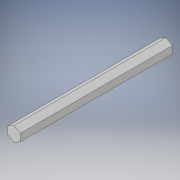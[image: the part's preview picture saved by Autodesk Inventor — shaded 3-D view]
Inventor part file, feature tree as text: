
AUTODESK INVENTOR PART (.ipt)
format: ipt  version: 2018 (Build 220112000, 112)  size: 101,376 bytes
history: native  units: in
note: dims shown in document units (in); Inventor stores cm internally (conversion verified against a paired STEP export)
features: extrude x1, sketch x1
ambient origin geometry x8: Origin, YZ Plane, XZ Plane, XY Plane, X Axis, Y Axis, Z Axis, Center Point
bodies: Solid1 (feature_tree)
feature tree (2):
  extrude  "Extrusion1"  Depth=6.0in
  sketch  "Sketch1"  dims[d0=6.0in d1=0.0in d5=0.25in]
